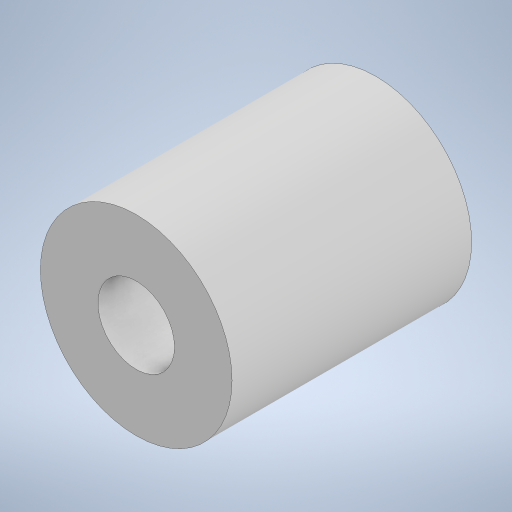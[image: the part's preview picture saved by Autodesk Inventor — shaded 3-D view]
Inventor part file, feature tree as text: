
AUTODESK INVENTOR PART (.ipt)
format: ipt  version: 2023.1 (Build 271208000, 208)  size: 209,920 bytes
history: native  units: mm
features: extrude x3, sketch x2
ambient origin geometry x8: Origin, YZ Plane, XZ Plane, XY Plane, X Axis, Y Axis, Z Axis, Center Point
bodies: Solid1 (feature_tree)
feature tree (5):
  extrude  "Extrusion1"  Depth=25.0mm TaperAngle=0.0deg
  sketch  "Sketch2"  dims[d5=5.0mm d6=8.0mm d7=0.0mm d8=0.0mm d9=17.0mm d10=0.0mm]
  extrude  "Extrusion2"  Depth=8.0mm
  extrude  "Extrusion3"  TaperAngle=0.0deg  [1 undecoded]
  sketch  "Sketch1"  dims[d0=20.0mm d1=25.0mm d2=0.0mm]
note: 1 required parameter value undecoded (feature->parameter linkage not recoverable at this tier; creation-order binding heuristic only, values carry confidence <= 0.55)
